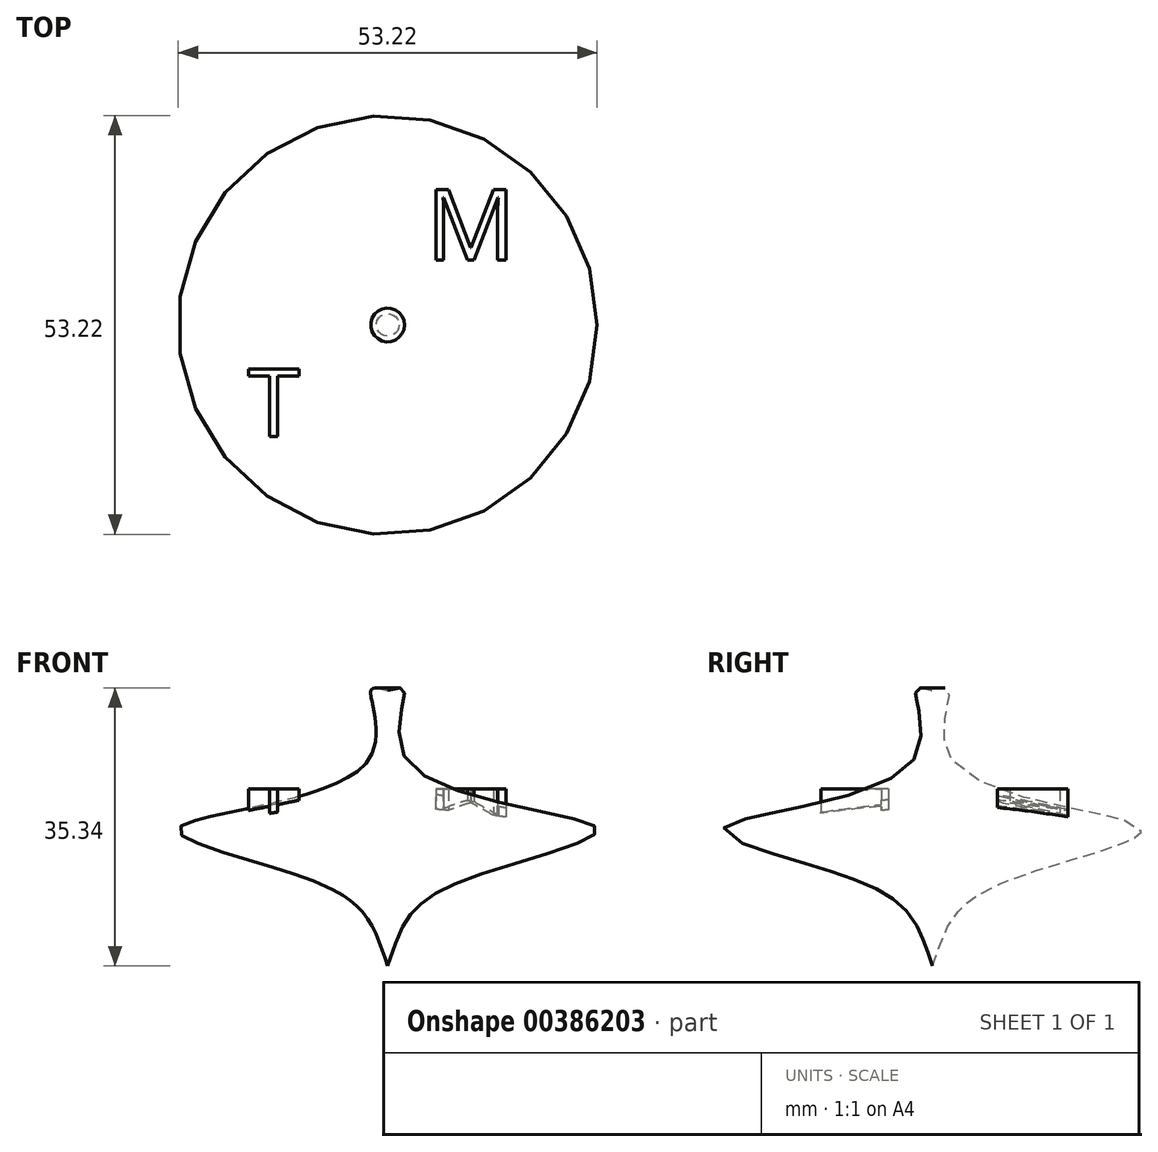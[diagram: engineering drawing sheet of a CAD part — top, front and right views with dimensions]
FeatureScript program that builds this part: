
annotation { "Feature Type Name" : "Feature", "Feature Type Description" : "" }
export const myFeature = defineFeature(function(context is Context, id is Id, definition is map)
    precondition{}
    {
        {
            var Q0;
            Q0=qCreatedBy(makeId("Front.planeOp"),FACE);
            var sketch = newSketch(context, id + "F0", { "sketchPlane" : qUnion([Q0])});
            skPoint(sketch, "E0", {"position": v(0, 0) * mm});
            skLineSegment(sketch, "E1", {"start": v(0, 17.5) * mm, "end": v(0, -17.5) * mm});
            skLineSegment(sketch, "E2", {"start": v(-25, 0) * mm, "end": v(25, 0) * mm});
            skFitSpline(sketch, "E3", {"points": [v(0, 17.5) * mm, v(2.12, 17.5) * mm, v(2.7, 8.33) * mm, v(26.54, 0) * mm, v(12.05, -5.74) * mm, v(3.25, -10.55) * mm, v(0, -17.5) * mm], "startDerivative": vector(46.27, 13.01) * mm, "endDerivative": vector(-26.54, -77.71) * mm});
            skLineSegment(sketch, "E4", {"start": v(0, 20.48) * mm, "end": v(0, -23.18) * mm});
            skSolve(sketch);
        }
        {
            var Q0;
            {var subQ0=sQuery(id+"F0.wireOp",EDGE,"E3");Q0=makeQuery(id+"F0.imprint","IMPRINT",FACE,{"disambiguationData":[TD([[makeQuery(id+"F0.imprint","IMPRINT",EDGE,{"derivedFrom":subQ0}),-1.0]])]});}
            var Q1;
            Q1=sQuery(id+"F0.wireOp",EDGE,"E4");
            revolve(context, id + "F1", {"entities" : qUnion([Q0]), "axis" : qUnion([Q1]), "revolveType" : RevolveType.FULL});
        }
        {
            var Q0;
            Q0=qCreatedBy(makeId("Top.planeOp"),FACE);
            var sketch = newSketch(context, id + "F2", { "sketchPlane" : qUnion([Q0])});
            skText(sketch, "E5", { "text": "M", "fontName": "OpenSans-Regular.ttf"});
            skText(sketch, "E6", { "text": "T", "fontName": "OpenSans-Regular.ttf"});
            const initialGuessF2  = {"E5": [0.00494, 0.00825, 1, 0, 0.009], "E6": [-0.01777, -0.01415, 1, 0, 0.00859]};
            skSetInitialGuess(sketch, initialGuessF2);
            skSolve(sketch);
        }
        {
            var Q0;
            Q0 = qSketchRegion(id + "F2", true);
            extrude(context, id + "F3", {"entities" : qUnion([Q0]), "operationType" : NewBodyOperationType.ADD, "depth" : 5 * mm});
        }
    });
